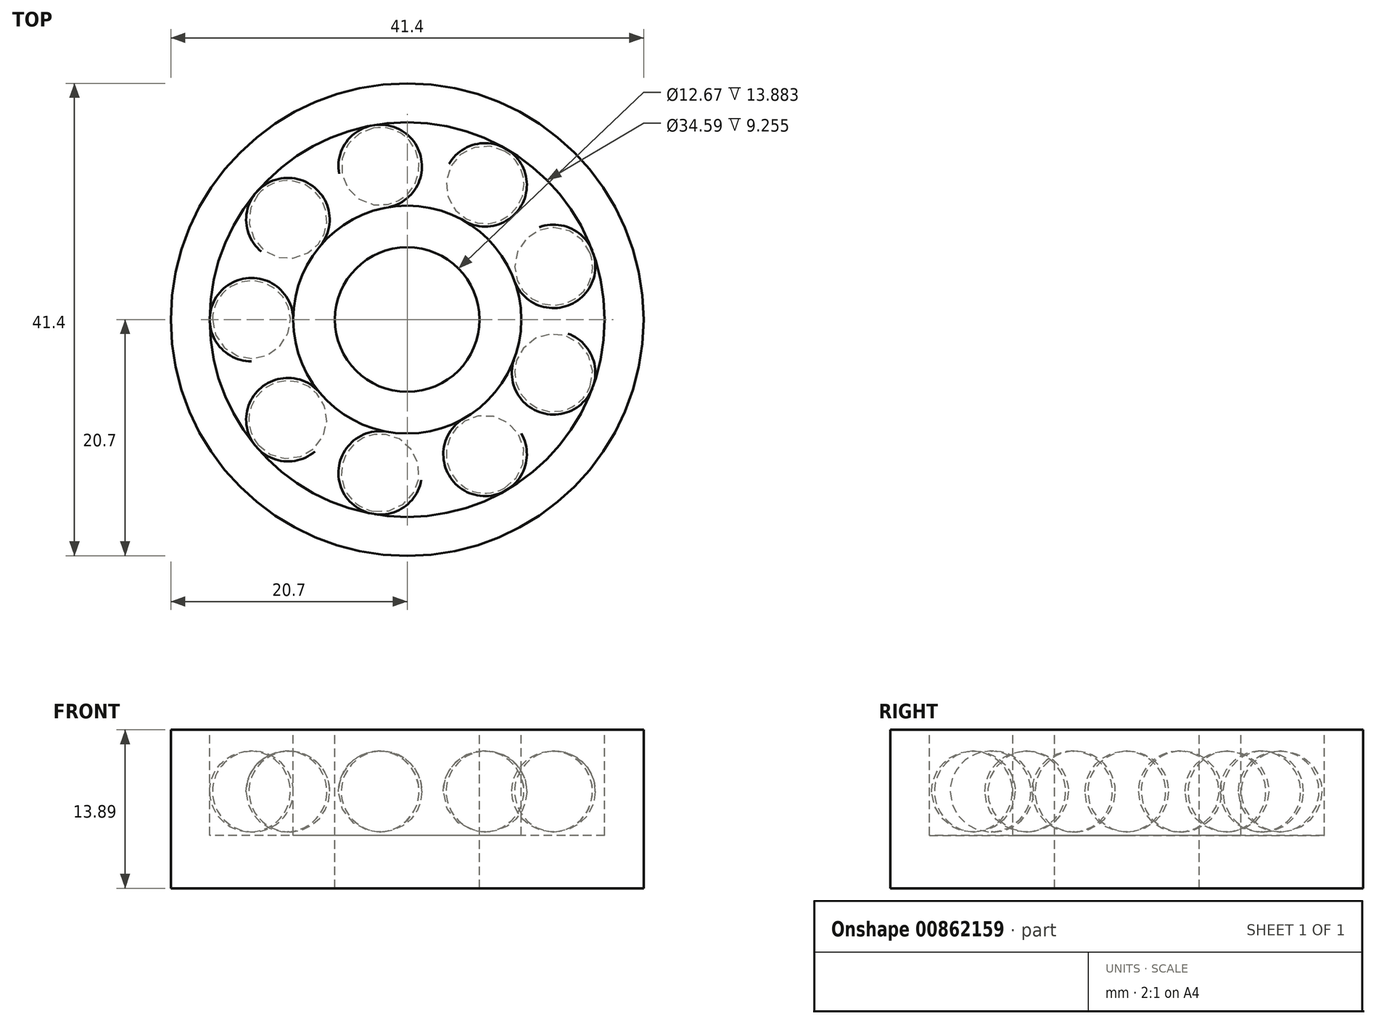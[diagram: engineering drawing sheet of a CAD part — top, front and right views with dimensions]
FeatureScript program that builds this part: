
annotation { "Feature Type Name" : "Feature", "Feature Type Description" : "" }
export const myFeature = defineFeature(function(context is Context, id is Id, definition is map)
    precondition{}
    {
        {
            var Q0;
            Q0=qCreatedBy(makeId("Front.planeOp"),FACE);
            var sketch = newSketch(context, id + "F0", { "sketchPlane" : qUnion([Q0])});
            skLineSegment(sketch, "E0.bottom", {"start": v(-20.7, 9.26) * mm, "end": v(-17.3, 9.26) * mm});
            skLineSegment(sketch, "E0.top", {"start": v(-20.7, -4.63) * mm, "end": v(-17.3, -4.63) * mm});
            skLineSegment(sketch, "E0.left", {"start": v(-20.7, 9.26) * mm, "end": v(-20.7, -4.63) * mm});
            skLineSegment(sketch, "E0.right", {"start": v(-17.3, 9.26) * mm, "end": v(-17.3, -4.63) * mm});
            skLineSegment(sketch, "E1.bottom", {"start": v(-17.3, -4.63) * mm, "end": v(-6.33, -4.63) * mm});
            skLineSegment(sketch, "E1.top", {"start": v(-17.3, 0) * mm, "end": v(-6.33, 0) * mm});
            skLineSegment(sketch, "E1.left", {"start": v(-17.3, -4.63) * mm, "end": v(-17.3, 0) * mm});
            skLineSegment(sketch, "E1.right", {"start": v(-6.33, -4.63) * mm, "end": v(-6.33, 0) * mm});
            skLineSegment(sketch, "E2.bottom", {"start": v(-6.33, 0) * mm, "end": v(-9.99, 0) * mm});
            skLineSegment(sketch, "E2.top", {"start": v(-6.33, 9.26) * mm, "end": v(-9.99, 9.26) * mm});
            skLineSegment(sketch, "E2.left", {"start": v(-6.33, 0) * mm, "end": v(-6.33, 9.26) * mm});
            skLineSegment(sketch, "E2.right", {"start": v(-9.99, 0) * mm, "end": v(-9.99, 9.26) * mm});
            skLineSegment(sketch, "E3", {"start": v(0, 32.15) * mm, "end": v(0, -30.69) * mm});
            skSolve(sketch);
        }
        {
            var Q0;
            Q0 = qSketchRegion(id + "F0", true);
            var Q1;
            Q1=sQuery(id+"F0.wireOp",EDGE,"E3");
            revolve(context, id + "F1", {"surfaceOperationType" : NewSurfaceOperationType.NEW, "entities" : qUnion([Q0]), "axis" : qUnion([Q1]), "revolveType" : RevolveType.FULL});
        }
        {
            var Q0;
            Q0=qCreatedBy(makeId("Front.planeOp"),FACE);
            var sketch = newSketch(context, id + "F2", { "sketchPlane" : qUnion([Q0])});
            skArc(sketch, "E4", {"start": v(-13.67, 7.38) * mm, "mid": v(-17.3, 3.82) * mm, "end": v(-13.61, 0.32) * mm});
            skLineSegment(sketch, "E5", {"start": v(-13.67, 7.38) * mm, "end": v(-13.61, 0.32) * mm});
            skSolve(sketch);
        }
        {
            var Q0;
            Q0 = qSketchRegion(id + "F2", true);
            var Q1;
            Q1=sQuery(id+"F2.wireOp",EDGE,"E5");
            revolve(context, id + "F3", {"surfaceOperationType" : NewSurfaceOperationType.NEW, "entities" : qUnion([Q0]), "axis" : qUnion([Q1]), "revolveType" : RevolveType.FULL});
        }
        {
            var Q0;
            Q0=makeQuery(id+"F3.opRevolve","SWEPT_BODY",BODY,{"disambiguationData":[OSD([sQuery(id+"F2.wireOp",EDGE,"E4"),sQuery(id+"F2.wireOp",EDGE,"E5")])]});
            var Q1;
            Q1=makeQuery(id+"F1.opRevolve","SWEPT_EDGE",EDGE,{"disambiguationData":[OSD([sQuery(id+"F0.wireOp",EDGE,"E0.bottom"),sQuery(id+"F0.wireOp",EDGE,"E0.right")])]});
            circularPattern(context, id + "F4", {"entities" : qUnion([Q0]), "axis" : qUnion([Q1]), "angle" : 360 * degree, "instanceCount" : 9, "equalSpace" : true});
        }
    });
